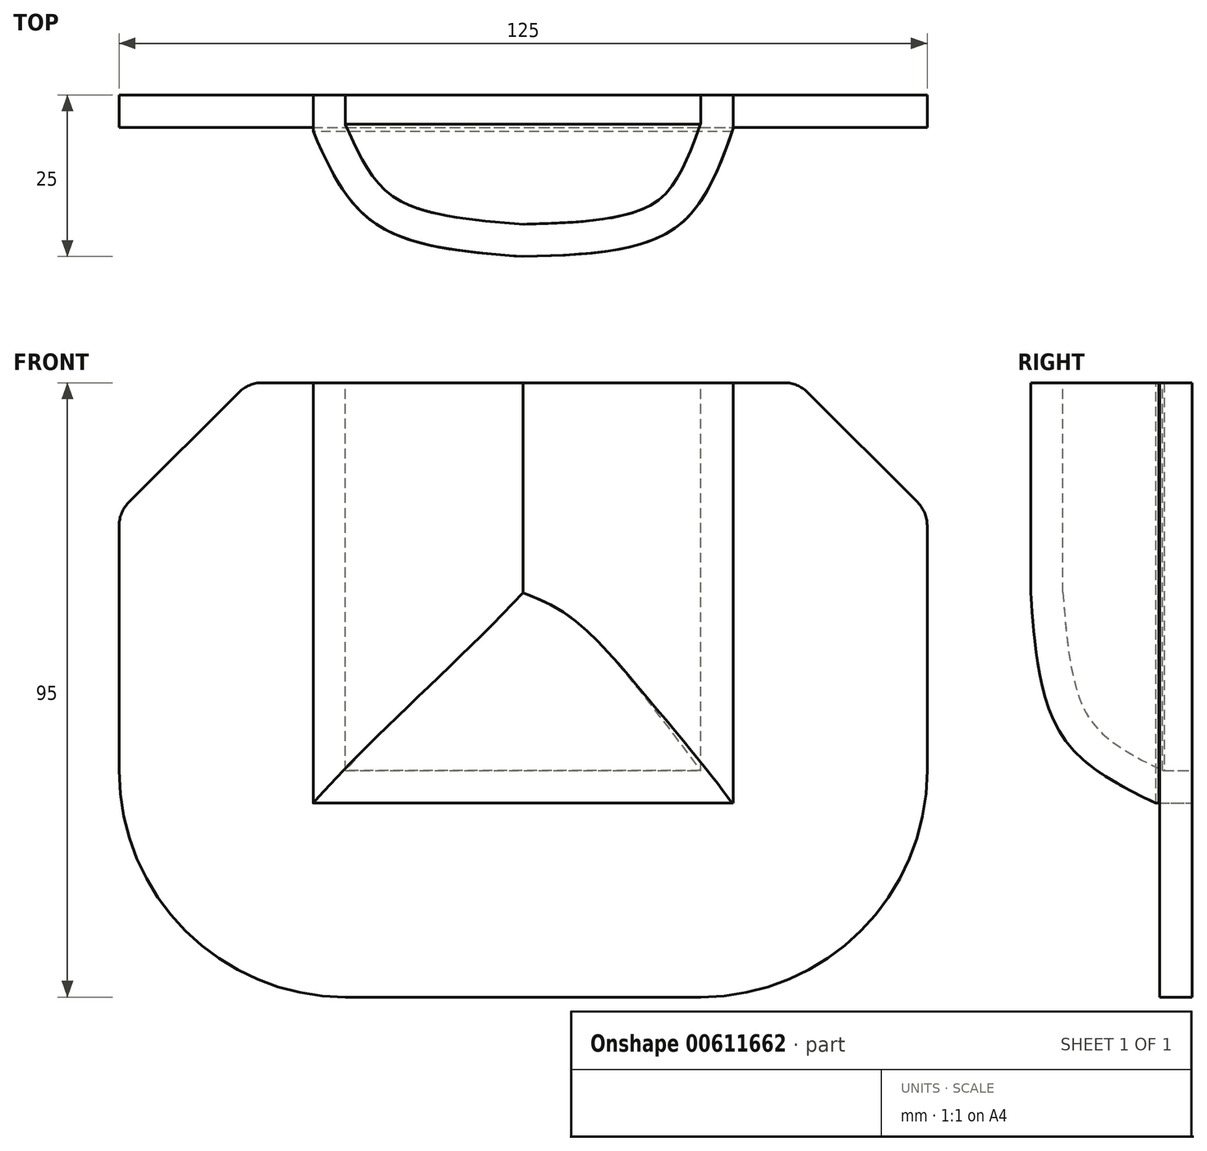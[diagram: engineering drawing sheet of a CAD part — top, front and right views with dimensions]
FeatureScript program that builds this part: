
annotation { "Feature Type Name" : "Feature", "Feature Type Description" : "" }
export const myFeature = defineFeature(function(context is Context, id is Id, definition is map)
    precondition{}
    {
        {
            var Q0;
            Q0=qCreatedBy(makeId("Front.planeOp"),FACE);
            var sketch = newSketch(context, id + "F0", { "sketchPlane" : qUnion([Q0])});
            skLineSegment(sketch, "E0.bottom", {"start": v(-62.5, -47.5) * mm, "end": v(62.5, -47.5) * mm});
            skLineSegment(sketch, "E0.top", {"start": v(-62.5, 47.5) * mm, "end": v(62.5, 47.5) * mm});
            skLineSegment(sketch, "E0.left", {"start": v(-62.5, -47.5) * mm, "end": v(-62.5, 47.5) * mm});
            skLineSegment(sketch, "E0.right", {"start": v(62.5, -47.5) * mm, "end": v(62.5, 47.5) * mm});
            skPoint(sketch, "E0.middle", {"position": v(0, 0) * mm});
            skLineSegment(sketch, "E1.bottom", {"start": v(-32.5, -17.5) * mm, "end": v(32.5, -17.5) * mm});
            skLineSegment(sketch, "E1.top", {"start": v(-32.5, 17.5) * mm, "end": v(32.5, 17.5) * mm});
            skLineSegment(sketch, "E1.left", {"start": v(-32.5, -17.5) * mm, "end": v(-32.5, 17.5) * mm});
            skLineSegment(sketch, "E1.right", {"start": v(32.5, -17.5) * mm, "end": v(32.5, 17.5) * mm});
            skLineSegment(sketch, "E2.bottom", {"start": v(32.5, 17.5) * mm, "end": v(-32.5, 17.5) * mm});
            skLineSegment(sketch, "E2.top", {"start": v(32.5, 47.5) * mm, "end": v(-32.5, 47.5) * mm});
            skLineSegment(sketch, "E2.left", {"start": v(32.5, 17.5) * mm, "end": v(32.5, 47.5) * mm});
            skLineSegment(sketch, "E2.right", {"start": v(-32.5, 17.5) * mm, "end": v(-32.5, 47.5) * mm});
            skSolve(sketch);
        }
        {
            var Q0;
            Q0=makeQuery(id+"F0.imprint","IMPRINT",FACE,{"disambiguationData":[TD([[makeQuery(id+"F0.imprint","IMPRINT",EDGE,{"derivedFrom":sQuery(id+"F0.wireOp",EDGE,"E0.bottom")}),1.0]])]});
            extrude(context, id + "F1", {"entities" : qUnion([Q0]), "depth" : 5 * mm, "offsetDistance" : 25 * mm});
        }
        {
            var Q0;
            Q0=makeQuery(id+"F1.opExtrude","CAP_FACE",FACE,{"disambiguationData":[OSD([sQuery(id+"F0.wireOp",EDGE,"E0.bottom"),sQuery(id+"F0.wireOp",EDGE,"E0.top"),sQuery(id+"F0.wireOp",EDGE,"E0.left"),sQuery(id+"F0.wireOp",EDGE,"E0.right"),sQuery(id+"F0.wireOp",EDGE,"E1.bottom"),sQuery(id+"F0.wireOp",EDGE,"E1.left"),sQuery(id+"F0.wireOp",EDGE,"E1.right"),sQuery(id+"F0.wireOp",EDGE,"E2.left"),sQuery(id+"F0.wireOp",EDGE,"E2.right")])],"isStart":true});
            var sketch = newSketch(context, id + "F2", { "sketchPlane" : qUnion([Q0])});
            skLineSegment(sketch, "E3.bottom", {"start": v(-32.5, -17.5) * mm, "end": v(32.5, -17.5) * mm});
            skLineSegment(sketch, "E3.top", {"start": v(-32.5, 47.5) * mm, "end": v(32.5, 47.5) * mm});
            skLineSegment(sketch, "E3.left", {"start": v(-32.5, -17.5) * mm, "end": v(-32.5, 47.5) * mm});
            skLineSegment(sketch, "E3.right", {"start": v(32.5, -17.5) * mm, "end": v(32.5, 47.5) * mm});
            skSolve(sketch);
        }
        {
            var Q0;
            Q0=makeQuery(id+"F2.imprint","IMPRINT",FACE,{"disambiguationData":[TD([[makeQuery(id+"F2.imprint","IMPRINT",EDGE,{"derivedFrom":sQuery(id+"F2.wireOp",EDGE,"E3.bottom")}),-1.0]])]});
            extrude(context, id + "F3", {"entities" : qUnion([Q0]), "oppositeDirection" : true, "depth" : 25 * mm, "offsetDistance" : 25 * mm});
        }
        {
            var Q0;
            Q0=makeQuery(id+"F3.opExtrude","SWEPT_FACE",FACE,{"disambiguationData":[OSD([sQuery(id+"F2.wireOp",EDGE,"E3.top")])]});
            var sketch = newSketch(context, id + "F4", { "sketchPlane" : qUnion([Q0])});
            skFitSpline(sketch, "E4", {"points": [v(0, -25) * mm, v(-22.93, -19.86) * mm, v(-32.5, -5.63) * mm], "startDerivative": vector(-48.38, 3.77) * mm, "endDerivative": vector(-15.76, 35.8) * mm});
            skSolve(sketch);
        }
        {
            var Q0;
            Q0=makeQuery(id+"F3.opExtrude","SWEPT_FACE",FACE,{"disambiguationData":[OSD([sQuery(id+"F2.wireOp",EDGE,"E3.right")])]});
            var sketch = newSketch(context, id + "F5", { "sketchPlane" : qUnion([Q0])});
            skFitSpline(sketch, "E5", {"points": [v(25, 15) * mm, v(20.1, -7.13) * mm, v(5.68, -17.5) * mm], "startDerivative": vector(-3.53, -46.94) * mm, "endDerivative": vector(-35.78, -17.46) * mm});
            skSolve(sketch);
        }
        {
            var Q0;
            Q0=makeQuery(id+"F3.opExtrude","SWEPT_FACE",FACE,{"disambiguationData":[OSD([sQuery(id+"F2.wireOp",EDGE,"E3.bottom")])]});
            var sketch = newSketch(context, id + "F6", { "sketchPlane" : qUnion([Q0])});
            skFitSpline(sketch, "E6", {"points": [v(0, 25) * mm, v(23.46, 20.6) * mm, v(32.5, 5.19) * mm], "startDerivative": vector(50.27, -1.48) * mm, "endDerivative": vector(13.85, -39.05) * mm});
            skSolve(sketch);
        }
        {
            var Q0;
            {var subQ0=sQuery(id+"F6.wireOp",EDGE,"E6");Q0=makeQuery(id+"F6.imprint","IMPRINT",FACE,{"disambiguationData":[TD([[makeQuery(id+"F6.imprint","IMPRINT",EDGE,{"derivedFrom":subQ0}),1.0]])]});}
            extrude(context, id + "F7", {"entities" : qUnion([Q0]), "operationType" : NewBodyOperationType.REMOVE, "oppositeDirection" : true, "depth" : 65 * mm, "offsetDistance" : 25 * mm});
        }
        {
            var Q0;
            {var subQ0=sQuery(id+"F5.wireOp",EDGE,"E5");Q0=makeQuery(id+"F5.imprint","IMPRINT",FACE,{"disambiguationData":[TD([[makeQuery(id+"F5.imprint","IMPRINT",EDGE,{"derivedFrom":subQ0}),1.0]])]});}
            extrude(context, id + "F8", {"entities" : qUnion([Q0]), "operationType" : NewBodyOperationType.REMOVE, "oppositeDirection" : true, "depth" : 65 * mm, "offsetDistance" : 25 * mm});
        }
        {
            var Q0;
            {var subQ0=sQuery(id+"F4.wireOp",EDGE,"E4");Q0=makeQuery(id+"F4.imprint","IMPRINT",FACE,{"disambiguationData":[TD([[makeQuery(id+"F4.imprint","IMPRINT",EDGE,{"derivedFrom":subQ0}),1.0]])]});}
            extrude(context, id + "F9", {"entities" : qUnion([Q0]), "operationType" : NewBodyOperationType.REMOVE, "oppositeDirection" : true, "depth" : 65 * mm, "offsetDistance" : 25 * mm});
        }
        {
            var Q0;
            Q0=makeQuery(id+"F1.opExtrude","SWEPT_EDGE",EDGE,{"disambiguationData":[OSD([sQuery(id+"F0.wireOp",EDGE,"E0.bottom"),sQuery(id+"F0.wireOp",EDGE,"E0.left")])]});
            fillet(context, id + "F10", {"entities" : qUnion([Q0]), "radius" : 35 * mm, "tangentPropagation" : true, "allowEdgeOverflow" : false});
        }
        {
            var Q0;
            Q0=makeQuery(id+"F1.opExtrude","SWEPT_EDGE",EDGE,{"disambiguationData":[OSD([sQuery(id+"F0.wireOp",EDGE,"E0.bottom"),sQuery(id+"F0.wireOp",EDGE,"E0.right")])]});
            fillet(context, id + "F11", {"entities" : qUnion([Q0]), "radius" : 35 * mm, "tangentPropagation" : true, "allowEdgeOverflow" : false});
        }
        {
            var Q0;
            Q0=makeQuery(id+"F1.opExtrude","SWEPT_EDGE",EDGE,{"disambiguationData":[OSD([sQuery(id+"F0.wireOp",EDGE,"E0.top"),sQuery(id+"F0.wireOp",EDGE,"E0.right")])]});
            chamfer(context, id + "F12", {"entities" : qUnion([Q0]), "width" : 20 * mm, "tangentPropagation" : true});
        }
        {
            var Q0;
            Q0=makeQuery(id+"F1.opExtrude","SWEPT_EDGE",EDGE,{"disambiguationData":[OSD([sQuery(id+"F0.wireOp",EDGE,"E0.top"),sQuery(id+"F0.wireOp",EDGE,"E0.left")])]});
            chamfer(context, id + "F13", {"entities" : qUnion([Q0]), "width" : 20 * mm, "tangentPropagation" : true});
        }
        {
            var Q0;
            {var subQ0=sQuery(id+"F0.wireOp",EDGE,"E0.right");var subQ1=sQuery(id+"F0.wireOp",EDGE,"E0.top");Q0=makeQuery(id+"F12.opChamfer","BLEND_EDGE",EDGE,{"blendedFrom":[makeQuery(id+"F1.opExtrude","SWEPT_EDGE",EDGE,{"disambiguationData":[OSD([subQ1,subQ0])]}),makeQuery(id+"F1.opExtrude","SWEPT_FACE",FACE,{"disambiguationData":[OSD([subQ1]),TDD([makeQuery(id+"F0.imprint","IMPRINT",EDGE,{"disambiguationData":[TD([[makeQuery(id+"F0.imprint","INTERSECT",VERTEX,{"derivedFrom":[subQ1,subQ0]}),1.0]])],"derivedFrom":subQ1})])]})],"blendedInto":[makeQuery(id+"F1.opExtrude","SWEPT_FACE",FACE,{"disambiguationData":[OSD([subQ1]),TDD([makeQuery(id+"F0.imprint","IMPRINT",EDGE,{"disambiguationData":[TD([[makeQuery(id+"F0.imprint","INTERSECT",VERTEX,{"derivedFrom":[subQ1,subQ0]}),1.0]])],"derivedFrom":subQ1})])]})]});}
            var Q1;
            {var subQ0=sQuery(id+"F0.wireOp",EDGE,"E0.left");var subQ1=sQuery(id+"F0.wireOp",EDGE,"E0.top");Q1=makeQuery(id+"F13.opChamfer","BLEND_EDGE",EDGE,{"blendedFrom":[makeQuery(id+"F1.opExtrude","SWEPT_EDGE",EDGE,{"disambiguationData":[OSD([subQ1,subQ0])]}),makeQuery(id+"F1.opExtrude","SWEPT_FACE",FACE,{"disambiguationData":[OSD([subQ1]),TDD([makeQuery(id+"F0.imprint","IMPRINT",EDGE,{"disambiguationData":[TD([[makeQuery(id+"F0.imprint","INTERSECT",VERTEX,{"derivedFrom":[subQ1,subQ0]}),-1.0]])],"derivedFrom":subQ1})])]})],"blendedInto":[makeQuery(id+"F1.opExtrude","SWEPT_FACE",FACE,{"disambiguationData":[OSD([subQ1]),TDD([makeQuery(id+"F0.imprint","IMPRINT",EDGE,{"disambiguationData":[TD([[makeQuery(id+"F0.imprint","INTERSECT",VERTEX,{"derivedFrom":[subQ1,subQ0]}),-1.0]])],"derivedFrom":subQ1})])]})]});}
            var Q2;
            {var subQ0=sQuery(id+"F0.wireOp",EDGE,"E0.right");Q2=makeQuery(id+"F12.opChamfer","BLEND_EDGE",EDGE,{"blendedFrom":[makeQuery(id+"F1.opExtrude","SWEPT_EDGE",EDGE,{"disambiguationData":[OSD([sQuery(id+"F0.wireOp",EDGE,"E0.top"),subQ0])]}),makeQuery(id+"F1.opExtrude","SWEPT_FACE",FACE,{"disambiguationData":[OSD([subQ0])]})],"blendedInto":[makeQuery(id+"F1.opExtrude","SWEPT_FACE",FACE,{"disambiguationData":[OSD([subQ0])]})]});}
            var Q3;
            {var subQ0=sQuery(id+"F0.wireOp",EDGE,"E0.left");Q3=makeQuery(id+"F13.opChamfer","BLEND_EDGE",EDGE,{"blendedFrom":[makeQuery(id+"F1.opExtrude","SWEPT_EDGE",EDGE,{"disambiguationData":[OSD([sQuery(id+"F0.wireOp",EDGE,"E0.top"),subQ0])]}),makeQuery(id+"F1.opExtrude","SWEPT_FACE",FACE,{"disambiguationData":[OSD([subQ0])]})],"blendedInto":[makeQuery(id+"F1.opExtrude","SWEPT_FACE",FACE,{"disambiguationData":[OSD([subQ0])]})]});}
            fillet(context, id + "F14", {"entities" : qUnion([Q0, Q1, Q2, Q3]), "radius" : 5 * mm, "tangentPropagation" : true, "allowEdgeOverflow" : false});
        }
        {
            var Q0;
            Q0=makeQuery(id+"F3.opExtrude","SWEPT_FACE",FACE,{"disambiguationData":[OSD([sQuery(id+"F2.wireOp",EDGE,"E3.top")])]});
            var Q1;
            Q1=makeQuery(id+"F3.opExtrude","CAP_FACE",FACE,{"disambiguationData":[OSD([sQuery(id+"F2.wireOp",EDGE,"E3.bottom"),sQuery(id+"F2.wireOp",EDGE,"E3.top"),sQuery(id+"F2.wireOp",EDGE,"E3.left"),sQuery(id+"F2.wireOp",EDGE,"E3.right")])],"isStart":true});
            shell(context, id + "F15", {"entities" : qUnion([Q0, Q1]), "thickness" : 5 * mm});
        }
    });
